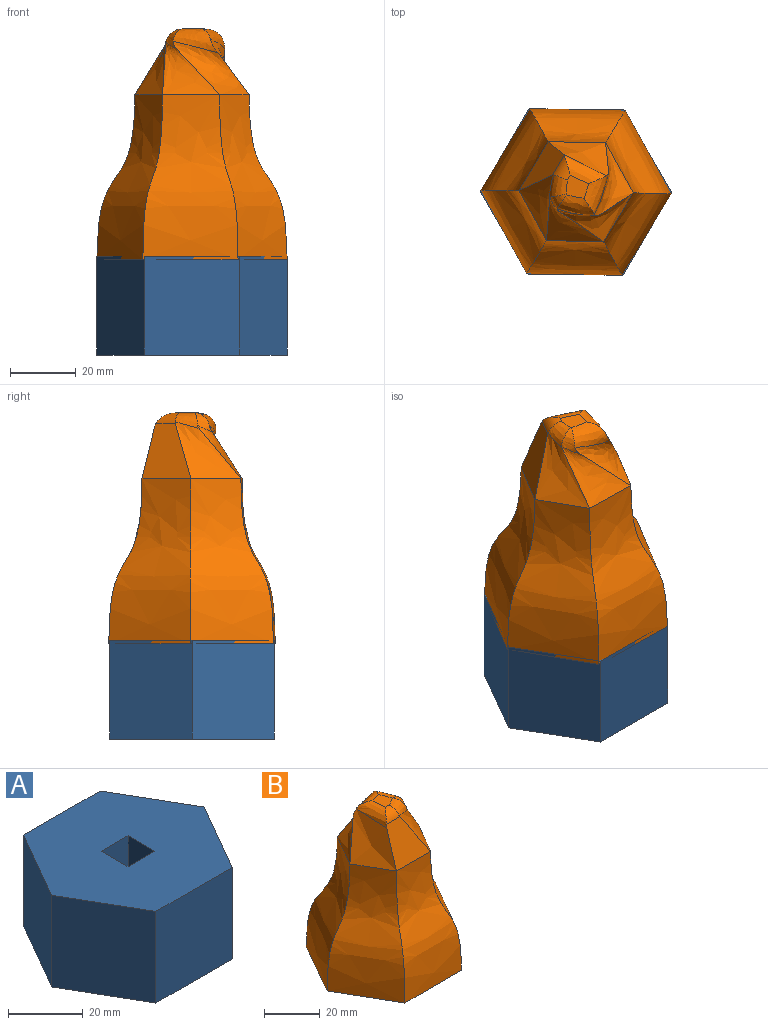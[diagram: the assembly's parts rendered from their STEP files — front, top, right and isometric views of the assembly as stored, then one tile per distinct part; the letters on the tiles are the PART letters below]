
ASSEMBLY  parts=2 mates=1
PART A: 15 faces, bbox 57.7x50x30 mm
  f0: plane 57.74x50mm, normal (0,0,1), area 2063.1mm2, adj f1,f2,f3,f4,f5,f6,f10,f11
  f1: plane 30x25mm, normal (-0.87,-0.5,0), area 866mm2, adj f0,f2,f6,f7
  f2: plane 30x28.87mm, normal (0,-1,0), area 866mm2, adj f0,f1,f3,f7
  f3: plane 30x25mm, normal (0.87,-0.5,0), area 866mm2, adj f0,f2,f4,f7
  f4: plane 30x25mm, normal (0.87,0.5,0), area 866mm2, adj f0,f3,f5,f7
  f5: plane 30x28.87mm, normal (0,1,0), area 866mm2, adj f0,f4,f6,f7
  f6: plane 30x25mm, normal (-0.87,0.5,0), area 866mm2, adj f0,f1,f5,f7
  f7: plane 57.74x50mm, normal (0,0,-1), area 1850.9mm2, adj f1,f2,f3,f4,f5,f6,f8
  f8: cylinder r=10mm len=20mm, axis (0,0,-1), area 377mm2, adj f7,f9
  f9: plane 20x20mm, normal (0,0,-1), area 314.2mm2, adj f8
  f10: plane 10.1x10.1mm, normal (0,1,0), area 102mm2, adj f0,f11,f13,f14
  f11: plane 10.1x10.1mm, normal (-1,0,0), area 102mm2, adj f0,f10,f12,f14
  f12: plane 10.1x10.1mm, normal (0,-1,0), area 102mm2, adj f0,f11,f13,f14
  f13: plane 10.1x10.1mm, normal (1,0,0), area 102mm2, adj f0,f10,f12,f14
  f14: plane 10.1x10.1mm, normal (0,0,1), area 102mm2, adj f10,f11,f12,f13
PART B: 25 faces, bbox 57.8x50x79.9 mm
  f0: plane 9.8x9.8mm, normal (0,-1,0), area 96mm2, adj f1,f3,f4,f5
  f1: plane 9.8x9.8mm, normal (1,0,0), area 96mm2, adj f0,f2,f4,f5
  f2: plane 9.8x9.8mm, normal (0,1,0), area 96mm2, adj f1,f3,f4,f5
  f3: plane 9.8x9.8mm, normal (-1,0,0), area 96mm2, adj f0,f2,f4,f5
  f4: plane 9.8x9.8mm, normal (0,0,-1), area 96mm2, adj f0,f1,f2,f3
  f5: plane 57.74x50mm, normal (0,0,-1), area 2069mm2, adj f0,f1,f2,f3,f6,f7,f8,f9
  f6: bspline ~50x28.87mm, area 1195.1mm2, adj f5,f7,f11,f13
  f7: bspline ~50x25mm, area 1195.1mm2, adj f5,f6,f8,f14
  f8: bspline ~50x25mm, area 1195.1mm2, adj f5,f7,f9,f15
  f9: bspline ~50x28.87mm, area 1195.1mm2, adj f5,f8,f10,f16
  f10: bspline ~50x25mm, area 1195.1mm2, adj f5,f9,f11,f17
  f11: bspline ~50x25mm, area 1195.1mm2, adj f5,f6,f10,f18
  f12: plane 7.18x6.32mm, normal (0,0,1), area 33.1mm2, adj f19,f20,f21,f22,f23,f24
  f13: plane 17.34x16.78mm, normal (0,-0.94,0.35), area 217.5mm2, adj f6,f14,f18,f23,f24
  f14: bspline ~20x19.82mm, area 211.6mm2, adj f7,f13,f15,f21,f23
  f15: bspline ~22.5x20mm, area 182.8mm2, adj f8,f14,f16,f19,f21
  f16: bspline ~22.5x20mm, area 221.4mm2, adj f9,f15,f17,f19,f20
  f17: bspline ~24.82x20mm, area 251.6mm2, adj f10,f16,f18,f20,f22
  f18: bspline ~22.5x20mm, area 280.2mm2, adj f11,f13,f17,f22,f24
  f19: bspline ~8.37x8.04mm, area 21.5mm2, adj f12,f15,f16,f20,f21
  f20: bspline ~18.15x10.23mm, area 77.3mm2, adj f12,f16,f17,f19,f22
  f21: bspline ~9.8x7.54mm, area 37.1mm2, adj f12,f14,f15,f19,f23
  f22: bspline ~19.15x8.33mm, area 67.9mm2, adj f12,f17,f18,f20,f24
  f23: cylinder r=5mm len=6.84mm, axis (1,0,0), area 27.3mm2, adj f12,f13,f14,f21,f24
  f24: bspline ~17.25x6.2mm, area 67.7mm2, adj f12,f13,f18,f22,f23
PLACE A t=(19.49,13.77,-58.65)mm fixed
PLACE B rot(axis=(0,0,-1),121.1deg) t=(19.49,13.77,-29.77)mm
MATE cylindrical B.f4 <-> A.f8  axis (0,0,-1) through (19.49,13.77,-39.57)mm
